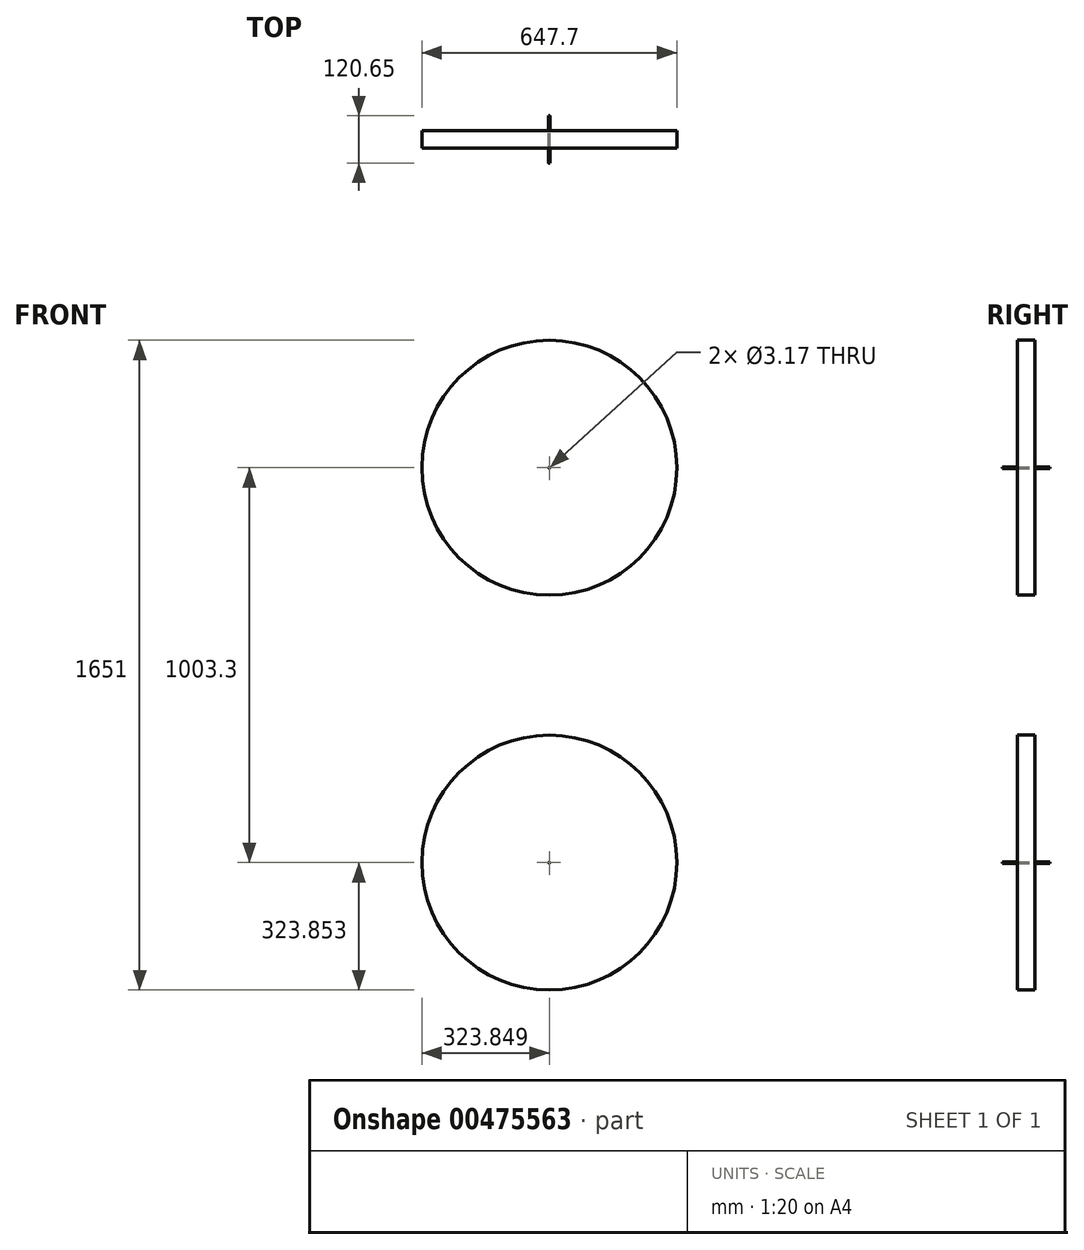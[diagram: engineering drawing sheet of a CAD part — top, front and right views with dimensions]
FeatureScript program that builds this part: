
annotation { "Feature Type Name" : "Feature", "Feature Type Description" : "" }
export const myFeature = defineFeature(function(context is Context, id is Id, definition is map)
    precondition{}
    {
        {
            var Q0;
            Q0=qCreatedBy(makeId("Front.planeOp"),FACE);
            var sketch = newSketch(context, id + "F0", { "sketchPlane" : qUnion([Q0])});
            skCircle(sketch, "E0", {"center": v(-481.95, 252.65) * mm, "radius": 323.85 * mm});
            skCircle(sketch, "E1", {"center": v(-481.95, 252.65) * mm, "radius": 1.59 * mm});
            skSolve(sketch);
        }
        {
            var Q0;
            Q0 = qSketchRegion(id + "F0", true);
            extrude(context, id + "F1", {"entities" : qUnion([Q0]), "depth" : 44.45 * mm, "offsetDistance" : 25.4 * mm});
        }
        {
            var Q0;
            Q0=makeQuery(id+"F0.imprint","IMPRINT",FACE,{"disambiguationData":[TD([[makeQuery(id+"F0.imprint","IMPRINT",EDGE,{"derivedFrom":sQuery(id+"F0.wireOp",EDGE,"E1")}),1.0]])]});
            extrude(context, id + "F2", {"entities" : qUnion([Q0]), "depth" : 82.55 * mm, "offsetDistance" : 25.4 * mm, "hasSecondDirection" : true, "secondDirectionOppositeDirection" : true, "secondDirectionDepth" : 38.1 * mm});
        }
        {
            var Q0;
            Q0=makeQuery(id+"F2.opExtrude","SWEPT_BODY",BODY,{"disambiguationData":[OSD([sQuery(id+"F0.wireOp",EDGE,"E1")])]});
            var Q1;
            Q1=makeQuery(id+"F1.opExtrude","SWEPT_BODY",BODY,{"disambiguationData":[OSD([sQuery(id+"F0.wireOp",EDGE,"E0"),sQuery(id+"F0.wireOp",EDGE,"E1")])]});
            transform(context, id + "F3", {"entities" : qUnion([Q0, Q1]), "transformType" : TransformType.TRANSLATION_3D, "dx" : 0 * mm, "dy" : 0 * mm, "dz" : 1003.3 * mm, "makeCopy" : true});
        }
    });
